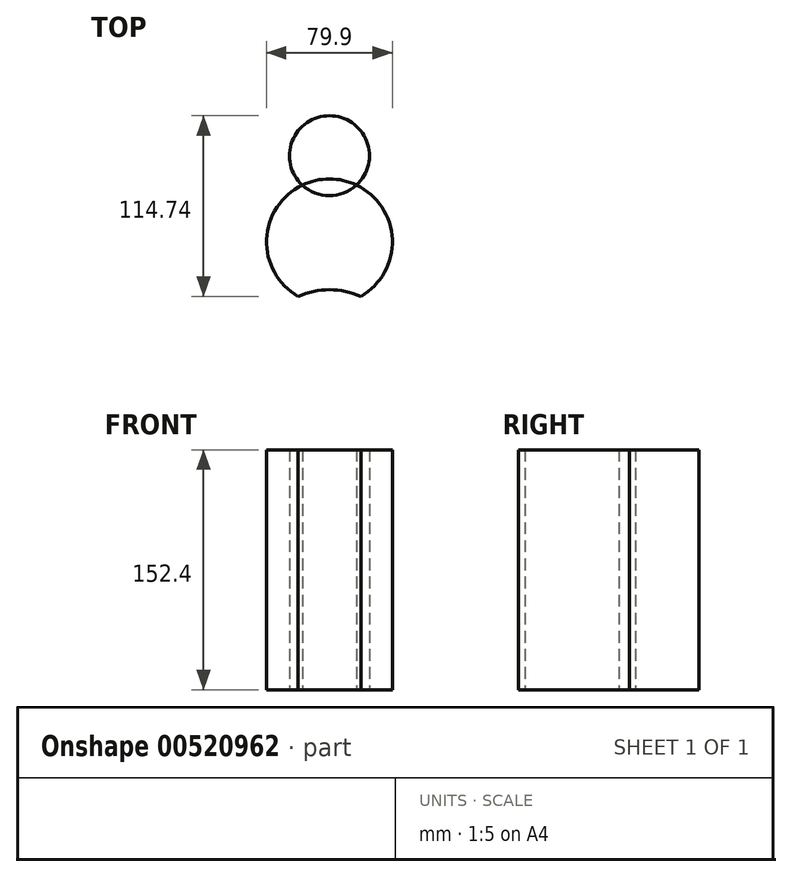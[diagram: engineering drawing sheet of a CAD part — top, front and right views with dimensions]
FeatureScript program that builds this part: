
annotation { "Feature Type Name" : "Feature", "Feature Type Description" : "" }
export const myFeature = defineFeature(function(context is Context, id is Id, definition is map)
    precondition{}
    {
        {
            var Q0;
            Q0=qCreatedBy(makeId("Top.planeOp"),FACE);
            var sketch = newSketch(context, id + "F0", { "sketchPlane" : qUnion([Q0])});
            skCircle(sketch, "E0", {"center": v(0, -52.07) * mm, "radius": 49.25 * mm});
            skCircle(sketch, "E1", {"center": v(0, 27.6) * mm, "radius": 39.95 * mm});
            skCircle(sketch, "E2", {"center": v(0, 82.3) * mm, "radius": 25.4 * mm});
            skSolve(sketch);
        }
        {
            var Q0;
            {var subQ0=sQuery(id+"F0.wireOp",EDGE,"E1");var subQ1=sQuery(id+"F0.wireOp",EDGE,"E0");var subQ2=makeQuery(id+"F0.imprint","INTERSECT",VERTEX,{"disambiguationData":[OD(0.0)],"derivedFrom":[subQ1,subQ0]});Q0=makeQuery(id+"F0.imprint","IMPRINT",FACE,{"disambiguationData":[TD([[makeQuery(id+"F0.imprint","IMPRINT",EDGE,{"disambiguationData":[TD([[subQ2,1.0]])],"derivedFrom":subQ1}),-1.0]])]});}
            var Q1;
            {var subQ0=sQuery(id+"F0.wireOp",EDGE,"E2");var subQ1=sQuery(id+"F0.wireOp",EDGE,"E1");var subQ2=makeQuery(id+"F0.imprint","INTERSECT",VERTEX,{"disambiguationData":[OD(0.0)],"derivedFrom":[subQ1,subQ0]});Q1=makeQuery(id+"F0.imprint","IMPRINT",FACE,{"disambiguationData":[TD([[makeQuery(id+"F0.imprint","IMPRINT",EDGE,{"disambiguationData":[TD([[subQ2,1.0]])],"derivedFrom":subQ1}),-1.0]])]});}
            extrude(context, id + "F1", {"entities" : qUnion([Q0, Q1]), "depth" : 152.4 * mm, "offsetDistance" : 25.4 * mm});
        }
    });
